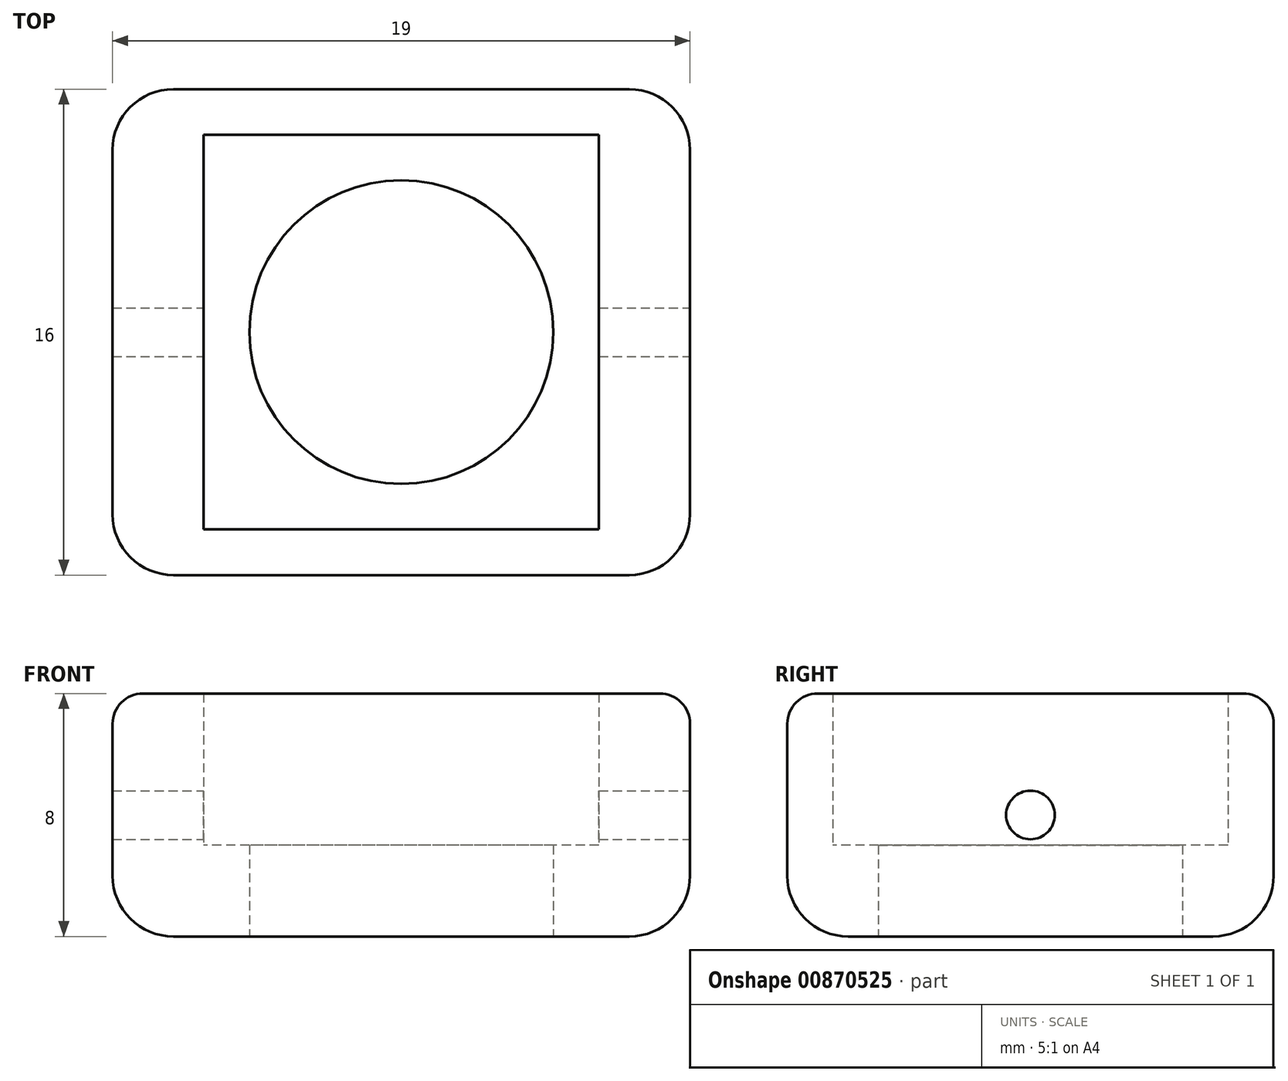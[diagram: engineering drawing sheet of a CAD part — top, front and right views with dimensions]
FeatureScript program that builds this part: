
annotation { "Feature Type Name" : "Feature", "Feature Type Description" : "" }
export const myFeature = defineFeature(function(context is Context, id is Id, definition is map)
    precondition{}
    {
        {
            var Q0;
            Q0=qCreatedBy(makeId("Top.planeOp"),FACE);
            var sketch = newSketch(context, id + "F0", { "sketchPlane" : qUnion([Q0])});
            skLineSegment(sketch, "E0.bottom", {"start": v(9.5, 8) * mm, "end": v(-9.5, 8) * mm});
            skLineSegment(sketch, "E0.top", {"start": v(9.5, -8) * mm, "end": v(-9.5, -8) * mm});
            skLineSegment(sketch, "E0.left", {"start": v(9.5, 8) * mm, "end": v(9.5, -8) * mm});
            skLineSegment(sketch, "E0.right", {"start": v(-9.5, 8) * mm, "end": v(-9.5, -8) * mm});
            skPoint(sketch, "E0.middle", {"position": v(0, 0) * mm});
            skCircle(sketch, "E1", {"center": v(0, 0) * mm, "radius": 5 * mm});
            skLineSegment(sketch, "E2.bottom", {"start": v(6.5, 6.5) * mm, "end": v(-6.5, 6.5) * mm});
            skLineSegment(sketch, "E2.top", {"start": v(6.5, -6.5) * mm, "end": v(-6.5, -6.5) * mm});
            skLineSegment(sketch, "E2.left", {"start": v(6.5, 6.5) * mm, "end": v(6.5, -6.5) * mm});
            skLineSegment(sketch, "E2.right", {"start": v(-6.5, 6.5) * mm, "end": v(-6.5, -6.5) * mm});
            skSolve(sketch);
        }
        {
            var Q0;
            Q0=makeQuery(id+"F0.imprint","IMPRINT",FACE,{"disambiguationData":[TD([[makeQuery(id+"F0.imprint","IMPRINT",EDGE,{"derivedFrom":sQuery(id+"F0.wireOp",EDGE,"E0.bottom")}),1.0]])]});
            var Q1;
            Q1=makeQuery(id+"F0.imprint","IMPRINT",FACE,{"disambiguationData":[TD([[makeQuery(id+"F0.imprint","IMPRINT",EDGE,{"derivedFrom":sQuery(id+"F0.wireOp",EDGE,"E1")}),-1.0]])]});
            extrude(context, id + "F1", {"entities" : qUnion([Q0, Q1]), "depth" : 3 * mm, "offsetDistance" : 25 * mm});
        }
        {
            var Q0;
            Q0=makeQuery(id+"F1.opExtrude","CAP_FACE",FACE,{"disambiguationData":[OSD([sQuery(id+"F0.wireOp",EDGE,"E0.bottom"),sQuery(id+"F0.wireOp",EDGE,"E0.top"),sQuery(id+"F0.wireOp",EDGE,"E0.left"),sQuery(id+"F0.wireOp",EDGE,"E0.right"),sQuery(id+"F0.wireOp",EDGE,"E1")])],"isStart":false});
            var sketch = newSketch(context, id + "F2", { "sketchPlane" : qUnion([Q0])});
            skLineSegment(sketch, "E3.bottom", {"start": v(6.5, 6.5) * mm, "end": v(-6.5, 6.5) * mm});
            skLineSegment(sketch, "E3.top", {"start": v(6.5, -6.5) * mm, "end": v(-6.5, -6.5) * mm});
            skLineSegment(sketch, "E3.left", {"start": v(6.5, 6.5) * mm, "end": v(6.5, -6.5) * mm});
            skLineSegment(sketch, "E3.right", {"start": v(-6.5, 6.5) * mm, "end": v(-6.5, -6.5) * mm});
            skPoint(sketch, "E3.middle", {"position": v(0, 0) * mm});
            skSolve(sketch);
        }
        {
            var Q0;
            Q0=makeQuery(id+"F2.imprint","IMPRINT",FACE,{"disambiguationData":[TD([[makeQuery(id+"F2.imprint","IMPRINT",EDGE,{"derivedFrom":sQuery(id+"F2.wireOp",EDGE,"E3.bottom")}),-1.0]])]});
            extrude(context, id + "F3", {"entities" : qUnion([Q0]), "operationType" : NewBodyOperationType.ADD, "depth" : 5 * mm, "offsetDistance" : 25 * mm});
        }
        {
            var Q0;
            {var subQ0=sQuery(id+"F0.wireOp",EDGE,"E0.left");Q0=makeQuery(id+"F3.boolean.opBoolean","MERGE",FACE,{"derivedFrom":[makeQuery(id+"F1.opExtrude","SWEPT_FACE",FACE,{"disambiguationData":[OSD([subQ0])]}),makeQuery(id+"F3.opExtrude","SWEPT_FACE",FACE,{"disambiguationData":[OSD([subQ0])]})]});}
            var sketch = newSketch(context, id + "F4", { "sketchPlane" : qUnion([Q0])});
            skLineSegment(sketch, "E4", {"start": v(0, 0) * mm, "end": v(0, 4) * mm});
            skCircle(sketch, "E5", {"center": v(0, 4) * mm, "radius": 0.8 * mm});
            skSolve(sketch);
        }
        {
            var Q0;
            Q0=sQuery(id+"F4.wireOp",VERTEX,"E5.center");
            var Q1;
            Q1=makeQuery(id+"F1.opExtrude","SWEPT_BODY",BODY,{"disambiguationData":[OSD([sQuery(id+"F0.wireOp",EDGE,"E0.bottom"),sQuery(id+"F0.wireOp",EDGE,"E0.top"),sQuery(id+"F0.wireOp",EDGE,"E0.left"),sQuery(id+"F0.wireOp",EDGE,"E0.right"),sQuery(id+"F0.wireOp",EDGE,"E1")])]});
            hole(context, id + "F5", {"style" : HoleStyle.SIMPLE, "endStyle" : HoleEndStyle.THROUGH, "holeDiameter" : 1.6 * mm, "majorDiameter" : 5 * mm, "isTappedThrough" : true, "tappedDepth" : 12 * mm, "tapClearance" : 3, "locations" : qUnion([Q0]), "scope" : qUnion([Q1])});
        }
        {
            var Q0;
            Q0=makeQuery(id+"F1.opExtrude","CAP_EDGE",EDGE,{"disambiguationData":[OSD([sQuery(id+"F0.wireOp",EDGE,"E0.top")])],"isStart":true});
            var Q1;
            Q1=makeQuery(id+"F1.opExtrude","CAP_EDGE",EDGE,{"disambiguationData":[OSD([sQuery(id+"F0.wireOp",EDGE,"E0.bottom")])],"isStart":true});
            var Q2;
            Q2=makeQuery(id+"F1.opExtrude","CAP_EDGE",EDGE,{"disambiguationData":[OSD([sQuery(id+"F0.wireOp",EDGE,"E0.right")])],"isStart":true});
            var Q3;
            Q3=makeQuery(id+"F1.opExtrude","CAP_EDGE",EDGE,{"disambiguationData":[OSD([sQuery(id+"F0.wireOp",EDGE,"E0.left")])],"isStart":true});
            fillet(context, id + "F6", {"entities" : qUnion([Q0, Q1, Q2, Q3]), "radius" : 2 * mm, "tangentPropagation" : true, "allowEdgeOverflow" : false});
        }
        {
            var Q0;
            {var subQ0=sQuery(id+"F0.wireOp",EDGE,"E0.left");var subQ1=sQuery(id+"F0.wireOp",EDGE,"E0.top");Q0=makeQuery(id+"F3.boolean.opBoolean","MERGE",EDGE,{"derivedFrom":[makeQuery(id+"F1.opExtrude","SWEPT_EDGE",EDGE,{"disambiguationData":[OSD([subQ1,subQ0])]}),makeQuery(id+"F3.opExtrude","SWEPT_EDGE",EDGE,{"disambiguationData":[OSD([subQ1,subQ0])]})]});}
            var Q1;
            {var subQ0=sQuery(id+"F0.wireOp",EDGE,"E0.left");var subQ1=sQuery(id+"F0.wireOp",EDGE,"E0.bottom");Q1=makeQuery(id+"F3.boolean.opBoolean","MERGE",EDGE,{"derivedFrom":[makeQuery(id+"F1.opExtrude","SWEPT_EDGE",EDGE,{"disambiguationData":[OSD([subQ1,subQ0])]}),makeQuery(id+"F3.opExtrude","SWEPT_EDGE",EDGE,{"disambiguationData":[OSD([subQ1,subQ0])]})]});}
            var Q2;
            {var subQ0=sQuery(id+"F0.wireOp",EDGE,"E0.right");var subQ1=sQuery(id+"F0.wireOp",EDGE,"E0.top");Q2=makeQuery(id+"F3.boolean.opBoolean","MERGE",EDGE,{"derivedFrom":[makeQuery(id+"F1.opExtrude","SWEPT_EDGE",EDGE,{"disambiguationData":[OSD([subQ1,subQ0])]}),makeQuery(id+"F3.opExtrude","SWEPT_EDGE",EDGE,{"disambiguationData":[OSD([subQ1,subQ0])]})]});}
            var Q3;
            {var subQ0=sQuery(id+"F0.wireOp",EDGE,"E0.right");var subQ1=sQuery(id+"F0.wireOp",EDGE,"E0.bottom");Q3=makeQuery(id+"F3.boolean.opBoolean","MERGE",EDGE,{"derivedFrom":[makeQuery(id+"F1.opExtrude","SWEPT_EDGE",EDGE,{"disambiguationData":[OSD([subQ1,subQ0])]}),makeQuery(id+"F3.opExtrude","SWEPT_EDGE",EDGE,{"disambiguationData":[OSD([subQ1,subQ0])]})]});}
            fillet(context, id + "F7", {"entities" : qUnion([Q0, Q1, Q2, Q3]), "radius" : 2 * mm, "tangentPropagation" : true, "allowEdgeOverflow" : false});
        }
        {
            var Q0;
            Q0=makeQuery(id+"F3.opExtrude","CAP_EDGE",EDGE,{"disambiguationData":[OSD([sQuery(id+"F0.wireOp",EDGE,"E0.bottom")])],"isStart":false});
            fillet(context, id + "F8", {"entities" : qUnion([Q0]), "radius" : 1 * mm, "tangentPropagation" : true, "allowEdgeOverflow" : false});
        }
    });
